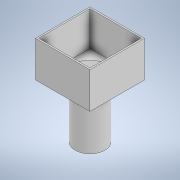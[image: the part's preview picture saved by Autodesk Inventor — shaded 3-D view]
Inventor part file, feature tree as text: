
AUTODESK INVENTOR PART (.ipt)
format: ipt  version: 2022 (Build 260153000, 153)  size: 159,744 bytes
history: native  units: in
note: dims shown in document units (in); Inventor stores cm internally (conversion verified against a paired STEP export)
features: sketch x5, extrude x4, chamfer x2, hole x1
ambient origin geometry x8: Origin, YZ Plane, XZ Plane, XY Plane, X Axis, Y Axis, Z Axis, Center Point
bodies: Solid1 (feature_tree)
feature tree (12):
  extrude  "Extrusion1"  Depth=2.047in
  extrude  "Extrusion2"  Depth=2.047in
  extrude  "Extrusion3"  Depth=2.047in
  extrude  "Extrusion4"  Depth=2.047in
  hole  "Hole1"  [1 undecoded]
  chamfer  "Chamfer1"  Distance=0.1181in
  chamfer  "Chamfer2"  Distance=2.165in
  sketch  "Sketch1"  dims[d0=2.047in d1=2.047in]
  sketch  "Sketch2"  dims[d2=2.047in d3=2.047in]
  sketch  "Sketch3"  dims[d4=2.047in d5=2.047in]
  sketch  "Sketch4"  dims[d6=2.047in d7=2.047in]
  sketch  "Sketch6"  dims[d8=2.047in d9=2.047in d10=0.1181in d11=0.0in d14=2.165in d15=2.165in d16=2.165in d17=2.165in d18=2.165in d19=2.165in d20=2.047in d21=2.047in d22=2.047in d23=2.047in d24=2.047in d25=2.047in d26=2.047in d27=2.047in d28=2.7559in d29=0.1181in d30=0.0in d31=0.0in d32=3.976in d33=0.7087in d34=0.0in d35=2.3622in d36=3.5433in d37=0.0in d39=2.165in d40=2.165in d41=0.75in d42=0.375in d43=0.25in d44=0.5635in d45=4.3701in d46=0.0in d47=0.8067in d48=0.7087in d49=45.0deg d50=0.6693in d51=0.7087in d52=45.0deg]
note: 1 required parameter value undecoded (feature->parameter linkage not recoverable at this tier; creation-order binding heuristic only, values carry confidence <= 0.55)
